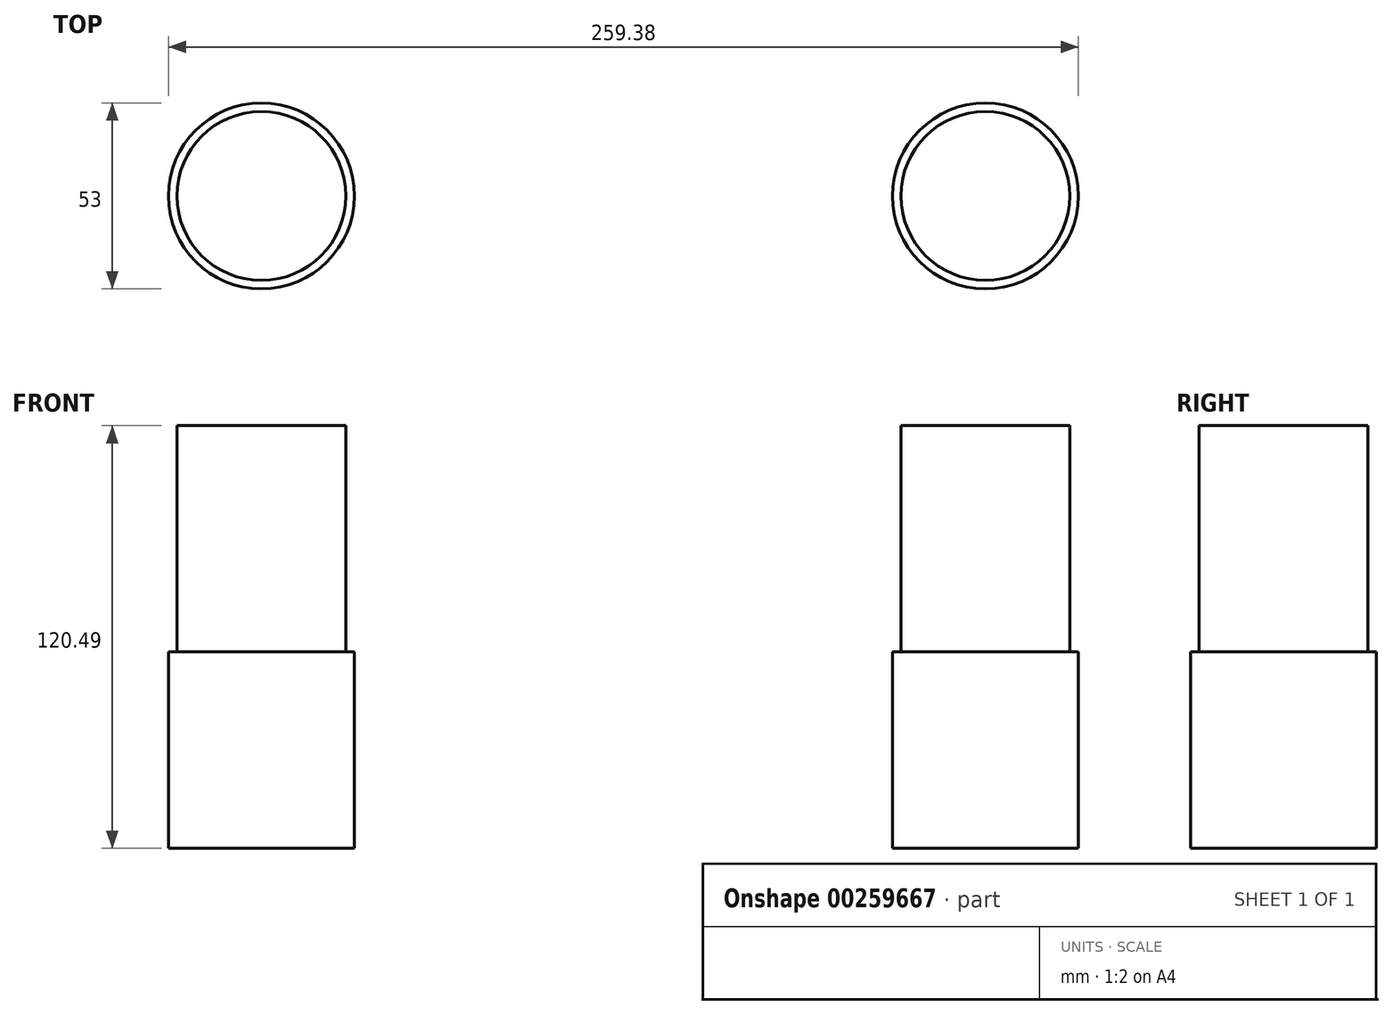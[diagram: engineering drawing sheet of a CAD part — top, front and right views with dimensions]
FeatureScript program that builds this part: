
annotation { "Feature Type Name" : "Feature", "Feature Type Description" : "" }
export const myFeature = defineFeature(function(context is Context, id is Id, definition is map)
    precondition{}
    {
        {
            var Q0;
            Q0=qCreatedBy(makeId("Front.planeOp"),FACE);
            var sketch = newSketch(context, id + "F0", { "sketchPlane" : qUnion([Q0])});
            skLineSegment(sketch, "E0", {"start": v(-103.19, 64.47) * mm, "end": v(-103.19, -56.02) * mm, "construction": true});
            skLineSegment(sketch, "E1", {"start": v(0, 0) * mm, "end": v(0, 86.61) * mm, "construction": true});
            skLineSegment(sketch, "E2.bottom", {"start": v(-103.19, 64.47) * mm, "end": v(-79.11, 64.47) * mm});
            skLineSegment(sketch, "E2.left", {"start": v(-103.19, 64.47) * mm, "end": v(-103.19, 0) * mm});
            skLineSegment(sketch, "E2.right", {"start": v(-79.11, 64.47) * mm, "end": v(-79.11, 0) * mm});
            skLineSegment(sketch, "E3.bottom", {"start": v(-79.11, 0) * mm, "end": v(-76.69, 0) * mm});
            skLineSegment(sketch, "E3.top", {"start": v(-103.19, -56.02) * mm, "end": v(-76.69, -56.02) * mm});
            skLineSegment(sketch, "E3.left", {"start": v(-103.19, 0) * mm, "end": v(-103.19, -56.02) * mm});
            skLineSegment(sketch, "E3.right", {"start": v(-76.69, 0) * mm, "end": v(-76.69, -56.02) * mm});
            skLineSegment(sketch, "E4", {"start": v(-103.19, 0) * mm, "end": v(-103.19, 113.37) * mm, "construction": true});
            skSolve(sketch);
        }
        {
            var Q0;
            Q0 = qSketchRegion(id + "F0", true);
            var Q1;
            Q1=sQuery(id+"F0.wireOp",EDGE,"E4");
            revolve(context, id + "F1", {"entities" : qUnion([Q0]), "axis" : qUnion([Q1]), "revolveType" : RevolveType.FULL});
        }
        {
            var Q0;
            Q0=makeQuery(id+"F1.opRevolve","SWEPT_BODY",BODY,{"disambiguationData":[OSD([sQuery(id+"F0.wireOp",EDGE,"E2.bottom"),sQuery(id+"F0.wireOp",EDGE,"E2.left"),sQuery(id+"F0.wireOp",EDGE,"E2.right"),sQuery(id+"F0.wireOp",EDGE,"E3.bottom"),sQuery(id+"F0.wireOp",EDGE,"E3.top"),sQuery(id+"F0.wireOp",EDGE,"E3.left"),sQuery(id+"F0.wireOp",EDGE,"E3.right")])]});
            var Q1;
            Q1=qCreatedBy(makeId("Right.planeOp"),FACE);
            mirror(context, id + "F2", {"entities" : qUnion([Q0]), "mirrorPlane" : qUnion([Q1])});
        }
    });
